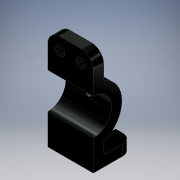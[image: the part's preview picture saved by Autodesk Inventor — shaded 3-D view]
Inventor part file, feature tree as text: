
AUTODESK INVENTOR PART (.ipt)
format: ipt  version: 2018 (Build 220112000, 112)  size: 171,520 bytes
history: native  units: mm
features: extrude x4, sketch x4, fillet x3, thread x1
ambient origin geometry x8: Origin, YZ Plane, XZ Plane, XY Plane, X Axis, Y Axis, Z Axis, Center Point
bodies: Solid1 (feature_tree)
feature tree (12):
  extrude  "Extrusion1"  Depth=51.0mm
  fillet  "Fillet1"  Radius=51.0mm
  fillet  "Fillet2"  Radius=11.0mm
  extrude  "Extrusion2"  Depth=48.0mm TaperAngle=0.0deg
  extrude  "Extrusion3"  Depth=10.0mm
  fillet  "Fillet3"  Radius=10.0mm
  extrude  "Extrusion4"  TaperAngle=0.0deg  [1 undecoded]
  thread  "Thread1"  [1 undecoded]
  sketch  "Sketch1"  dims[d0=41.0mm d1=107.0mm d2=51.0mm d3=11.0mm]
  sketch  "Sketch2"  dims[d4=30.0mm d5=48.0mm d6=0.0mm]
  sketch  "Sketch3"  dims[d7=13.0mm d8=2.0mm d9=10.0mm]
  sketch  "Sketch4"  dims[d10=10.0mm d11=0.0mm d12=0.0mm d14=13.0mm d17=16.0mm d18=16.0mm d19=0.0mm d20=0.0mm d21=10.0mm d22=5.0mm d23=41.0mm d24=0.0mm d25=10.0mm d26=0.0mm]
note: 2 required parameter values undecoded (feature->parameter linkage not recoverable at this tier; creation-order binding heuristic only, values carry confidence <= 0.55)
